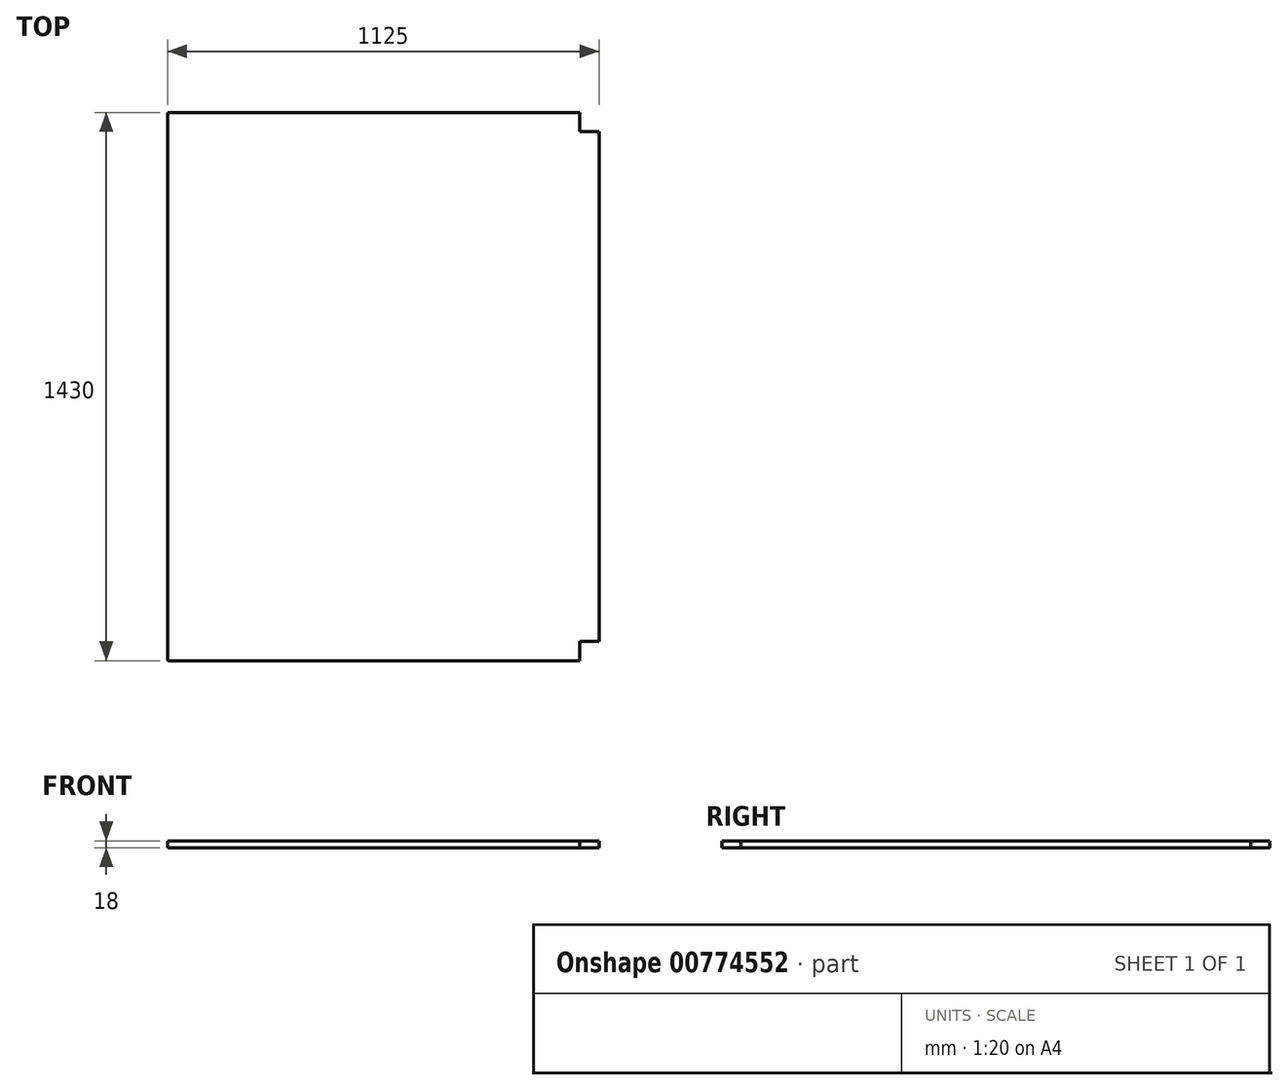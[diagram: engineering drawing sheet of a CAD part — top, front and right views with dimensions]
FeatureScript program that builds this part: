
annotation { "Feature Type Name" : "Feature", "Feature Type Description" : "" }
export const myFeature = defineFeature(function(context is Context, id is Id, definition is map)
    precondition{}
    {
        {
            var Q0;
            Q0=qCreatedBy(makeId("Front.planeOp"),FACE);
            var sketch = newSketch(context, id + "F0", { "sketchPlane" : qUnion([Q0])});
            skLineSegment(sketch, "E0.bottom", {"start": v(562.5, -9) * mm, "end": v(-562.5, -9) * mm});
            skLineSegment(sketch, "E0.top", {"start": v(562.5, 9) * mm, "end": v(-562.5, 9) * mm});
            skLineSegment(sketch, "E0.left", {"start": v(562.5, -9) * mm, "end": v(562.5, 9) * mm});
            skLineSegment(sketch, "E0.right", {"start": v(-562.5, -9) * mm, "end": v(-562.5, 9) * mm});
            skPoint(sketch, "E0.middle", {"position": v(0, 0) * mm});
            skSolve(sketch);
        }
        {
            var Q0;
            Q0 = qSketchRegion(id + "F0", true);
            extrude(context, id + "F1", {"entities" : qUnion([Q0]), "depth" : 1430 * mm, "offsetDistance" : 25 * mm});
        }
        {
            var Q0;
            Q0=makeQuery(id+"F1.opExtrude","SWEPT_FACE",FACE,{"disambiguationData":[OSD([sQuery(id+"F0.wireOp",EDGE,"E0.top")])]});
            var sketch = newSketch(context, id + "F2", { "sketchPlane" : qUnion([Q0])});
            skLineSegment(sketch, "E1.bottom", {"start": v(562.5, -1430) * mm, "end": v(512.5, -1430) * mm});
            skLineSegment(sketch, "E1.top", {"start": v(562.5, -1380) * mm, "end": v(512.5, -1380) * mm});
            skLineSegment(sketch, "E1.left", {"start": v(562.5, -1430) * mm, "end": v(562.5, -1380) * mm});
            skLineSegment(sketch, "E1.right", {"start": v(512.5, -1430) * mm, "end": v(512.5, -1380) * mm});
            skLineSegment(sketch, "E2.bottom", {"start": v(562.5, 0) * mm, "end": v(512.5, 0) * mm});
            skLineSegment(sketch, "E2.top", {"start": v(562.5, -50) * mm, "end": v(512.5, -50) * mm});
            skLineSegment(sketch, "E2.left", {"start": v(562.5, 0) * mm, "end": v(562.5, -50) * mm});
            skLineSegment(sketch, "E2.right", {"start": v(512.5, 0) * mm, "end": v(512.5, -50) * mm});
            skSolve(sketch);
        }
        {
            var Q0;
            Q0 = qSketchRegion(id + "F2", true);
            extrude(context, id + "F3", {"entities" : qUnion([Q0]), "operationType" : NewBodyOperationType.REMOVE, "endBound" : BoundingType.THROUGH_ALL, "oppositeDirection" : true, "depth" : 25 * mm, "offsetDistance" : 25 * mm});
        }
    });
